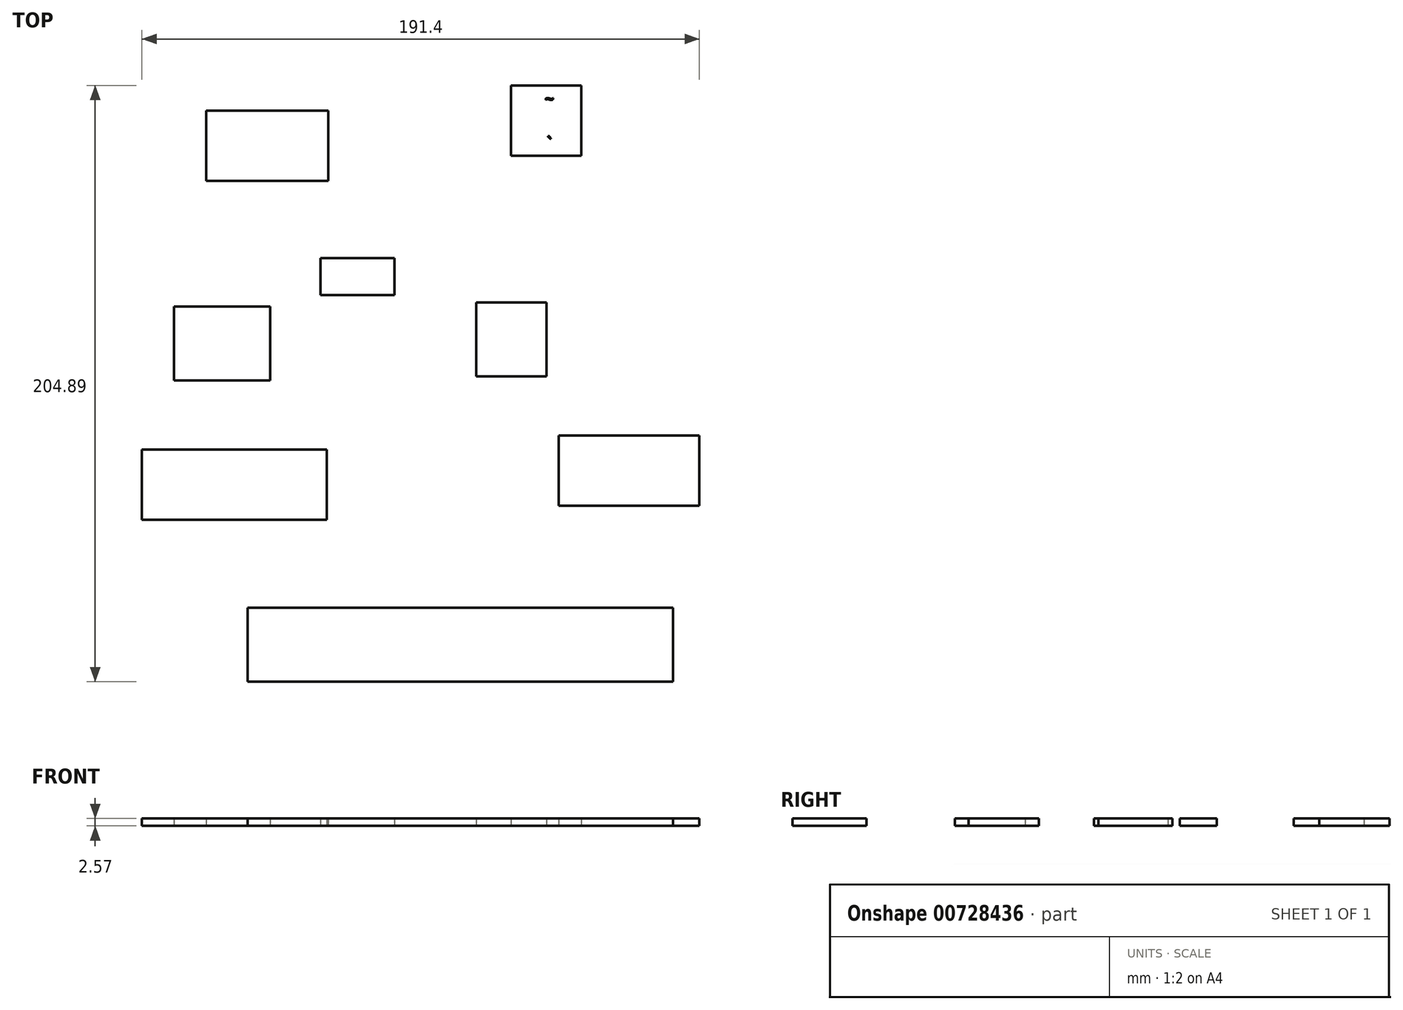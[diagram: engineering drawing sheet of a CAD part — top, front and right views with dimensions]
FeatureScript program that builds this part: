
annotation { "Feature Type Name" : "Feature", "Feature Type Description" : "" }
export const myFeature = defineFeature(function(context is Context, id is Id, definition is map)
    precondition{}
    {
        {
            var Q0;
            Q0=qCreatedBy(makeId("Top.planeOp"),FACE);
            var sketch = newSketch(context, id + "F0", { "sketchPlane" : qUnion([Q0])});
            skLineSegment(sketch, "E0.bottom", {"start": v(-24.02, 0) * mm, "end": v(1.38, 0) * mm});
            skLineSegment(sketch, "E0.top", {"start": v(-24.02, -12.7) * mm, "end": v(1.38, -12.7) * mm});
            skLineSegment(sketch, "E0.left", {"start": v(-24.02, 0) * mm, "end": v(-24.02, -12.7) * mm});
            skLineSegment(sketch, "E0.right", {"start": v(1.38, 0) * mm, "end": v(1.38, -12.7) * mm});
            skSolve(sketch);
        }
        {
            var Q0;
            Q0 = qSketchRegion(id + "F0", true);
            extrude(context, id + "F1", {"entities" : qUnion([Q0]), "depth" : 2.54 * mm, "offsetDistance" : 25.4 * mm});
        }
        {
            var Q0;
            Q0=qCreatedBy(makeId("Top.planeOp"),FACE);
            var sketch = newSketch(context, id + "F2", { "sketchPlane" : qUnion([Q0])});
            skLineSegment(sketch, "E1.bottom", {"start": v(41.35, 59.32) * mm, "end": v(65.48, 59.32) * mm});
            skLineSegment(sketch, "E1.top", {"start": v(41.35, 35.2) * mm, "end": v(65.48, 35.2) * mm});
            skLineSegment(sketch, "E1.left", {"start": v(41.35, 59.32) * mm, "end": v(41.35, 35.2) * mm});
            skLineSegment(sketch, "E1.right", {"start": v(65.48, 59.32) * mm, "end": v(65.48, 35.2) * mm});
            skSolve(sketch);
        }
        {
            var Q0;
            Q0 = qSketchRegion(id + "F2", true);
            extrude(context, id + "F3", {"entities" : qUnion([Q0]), "depth" : 2.54 * mm, "offsetDistance" : 25.4 * mm});
        }
        {
            var Q0;
            Q0=qCreatedBy(makeId("Top.planeOp"),FACE);
            var sketch = newSketch(context, id + "F4", { "sketchPlane" : qUnion([Q0])});
            skLineSegment(sketch, "E2.bottom", {"start": v(-63.25, 50.6) * mm, "end": v(-21.34, 50.6) * mm});
            skLineSegment(sketch, "E2.top", {"start": v(-63.25, 26.47) * mm, "end": v(-21.34, 26.47) * mm});
            skLineSegment(sketch, "E2.left", {"start": v(-63.25, 50.6) * mm, "end": v(-63.25, 26.47) * mm});
            skLineSegment(sketch, "E2.right", {"start": v(-21.34, 50.6) * mm, "end": v(-21.34, 26.47) * mm});
            skSolve(sketch);
        }
        {
            var Q0;
            Q0 = qSketchRegion(id + "F4", true);
            extrude(context, id + "F5", {"entities" : qUnion([Q0]), "depth" : 2.54 * mm, "offsetDistance" : 25.4 * mm});
        }
        {
            var Q0;
            Q0=qCreatedBy(makeId("Top.planeOp"),FACE);
            var sketch = newSketch(context, id + "F6", { "sketchPlane" : qUnion([Q0])});
            skLineSegment(sketch, "E3.bottom", {"start": v(57.83, -61) * mm, "end": v(106.1, -61) * mm});
            skLineSegment(sketch, "E3.top", {"start": v(57.83, -85.13) * mm, "end": v(106.1, -85.13) * mm});
            skLineSegment(sketch, "E3.left", {"start": v(57.83, -61) * mm, "end": v(57.83, -85.13) * mm});
            skLineSegment(sketch, "E3.right", {"start": v(106.1, -61) * mm, "end": v(106.1, -85.13) * mm});
            skSolve(sketch);
        }
        {
            var Q0;
            Q0 = qSketchRegion(id + "F6", true);
            extrude(context, id + "F7", {"entities" : qUnion([Q0]), "depth" : 2.54 * mm, "offsetDistance" : 25.4 * mm});
        }
        {
            var Q0;
            Q0=qCreatedBy(makeId("Top.planeOp"),FACE);
            var sketch = newSketch(context, id + "F8", { "sketchPlane" : qUnion([Q0])});
            skLineSegment(sketch, "E4.bottom", {"start": v(-85.31, -65.75) * mm, "end": v(-21.81, -65.75) * mm});
            skLineSegment(sketch, "E4.top", {"start": v(-85.31, -89.88) * mm, "end": v(-21.81, -89.88) * mm});
            skLineSegment(sketch, "E4.left", {"start": v(-85.31, -65.75) * mm, "end": v(-85.31, -89.88) * mm});
            skLineSegment(sketch, "E4.right", {"start": v(-21.81, -65.75) * mm, "end": v(-21.81, -89.88) * mm});
            skSolve(sketch);
        }
        {
            var Q0;
            Q0 = qSketchRegion(id + "F8", true);
            extrude(context, id + "F9", {"entities" : qUnion([Q0]), "depth" : 2.54 * mm, "offsetDistance" : 25.4 * mm});
        }
        {
            var Q0;
            Q0=qCreatedBy(makeId("Top.planeOp"),FACE);
            var sketch = newSketch(context, id + "F10", { "sketchPlane" : qUnion([Q0])});
            skLineSegment(sketch, "E5.bottom", {"start": v(29.42, -15.2) * mm, "end": v(53.55, -15.2) * mm});
            skLineSegment(sketch, "E5.top", {"start": v(29.42, -40.6) * mm, "end": v(53.55, -40.6) * mm});
            skLineSegment(sketch, "E5.left", {"start": v(29.42, -15.2) * mm, "end": v(29.42, -40.6) * mm});
            skLineSegment(sketch, "E5.right", {"start": v(53.55, -15.2) * mm, "end": v(53.55, -40.6) * mm});
            skSolve(sketch);
        }
        {
            var Q0;
            Q0 = qSketchRegion(id + "F10", true);
            extrude(context, id + "F11", {"entities" : qUnion([Q0]), "depth" : 2.54 * mm, "offsetDistance" : 25.4 * mm});
        }
        {
            var Q0;
            Q0=qCreatedBy(makeId("Top.planeOp"),FACE);
            var sketch = newSketch(context, id + "F12", { "sketchPlane" : qUnion([Q0])});
            skLineSegment(sketch, "E6.bottom", {"start": v(-74.26, -16.7) * mm, "end": v(-41.24, -16.7) * mm});
            skLineSegment(sketch, "E6.top", {"start": v(-74.26, -42.1) * mm, "end": v(-41.24, -42.1) * mm});
            skLineSegment(sketch, "E6.left", {"start": v(-74.26, -16.7) * mm, "end": v(-74.26, -42.1) * mm});
            skLineSegment(sketch, "E6.right", {"start": v(-41.24, -16.7) * mm, "end": v(-41.24, -42.1) * mm});
            skSolve(sketch);
        }
        {
            var Q0;
            Q0 = qSketchRegion(id + "F12", true);
            extrude(context, id + "F13", {"entities" : qUnion([Q0]), "depth" : 2.54 * mm, "offsetDistance" : 25.4 * mm});
        }
        {
            var Q0;
            Q0=qCreatedBy(makeId("Top.planeOp"),FACE);
            var sketch = newSketch(context, id + "F14", { "sketchPlane" : qUnion([Q0])});
            skLineSegment(sketch, "E7.bottom", {"start": v(-49.02, -120.17) * mm, "end": v(97.03, -120.17) * mm});
            skLineSegment(sketch, "E7.top", {"start": v(-49.02, -145.57) * mm, "end": v(97.03, -145.57) * mm});
            skLineSegment(sketch, "E7.left", {"start": v(-49.02, -120.17) * mm, "end": v(-49.02, -145.57) * mm});
            skLineSegment(sketch, "E7.right", {"start": v(97.03, -120.17) * mm, "end": v(97.03, -145.57) * mm});
            skSolve(sketch);
        }
        {
            var Q0;
            Q0 = qSketchRegion(id + "F14", true);
            extrude(context, id + "F15", {"entities" : qUnion([Q0]), "depth" : 2.54 * mm, "offsetDistance" : 25.4 * mm});
        }
        {
            var Q0;
            Q0=makeQuery(id+"F3.opExtrude","CAP_FACE",FACE,{"disambiguationData":[OSD([sQuery(id+"F2.wireOp",EDGE,"E1.bottom"),sQuery(id+"F2.wireOp",EDGE,"E1.top"),sQuery(id+"F2.wireOp",EDGE,"E1.left"),sQuery(id+"F2.wireOp",EDGE,"E1.right")])],"isStart":false});
            var sketch = newSketch(context, id + "F16", { "sketchPlane" : qUnion([Q0])});
            skText(sketch, "E8", { "text": "~\n\n`", "fontName": "OpenSans-Regular.ttf"});
            const initialGuessF16  = {"E8": [0.053, 0.0527, 1, 0, 0.004]};
            skSetInitialGuess(sketch, initialGuessF16);
            skSolve(sketch);
        }
        {
            var Q0;
            Q0 = qSketchRegion(id + "F16", true);
            extrude(context, id + "F17", {"entities" : qUnion([Q0]), "depth" : 0.03 * mm, "offsetDistance" : 25.4 * mm});
        }
    });
